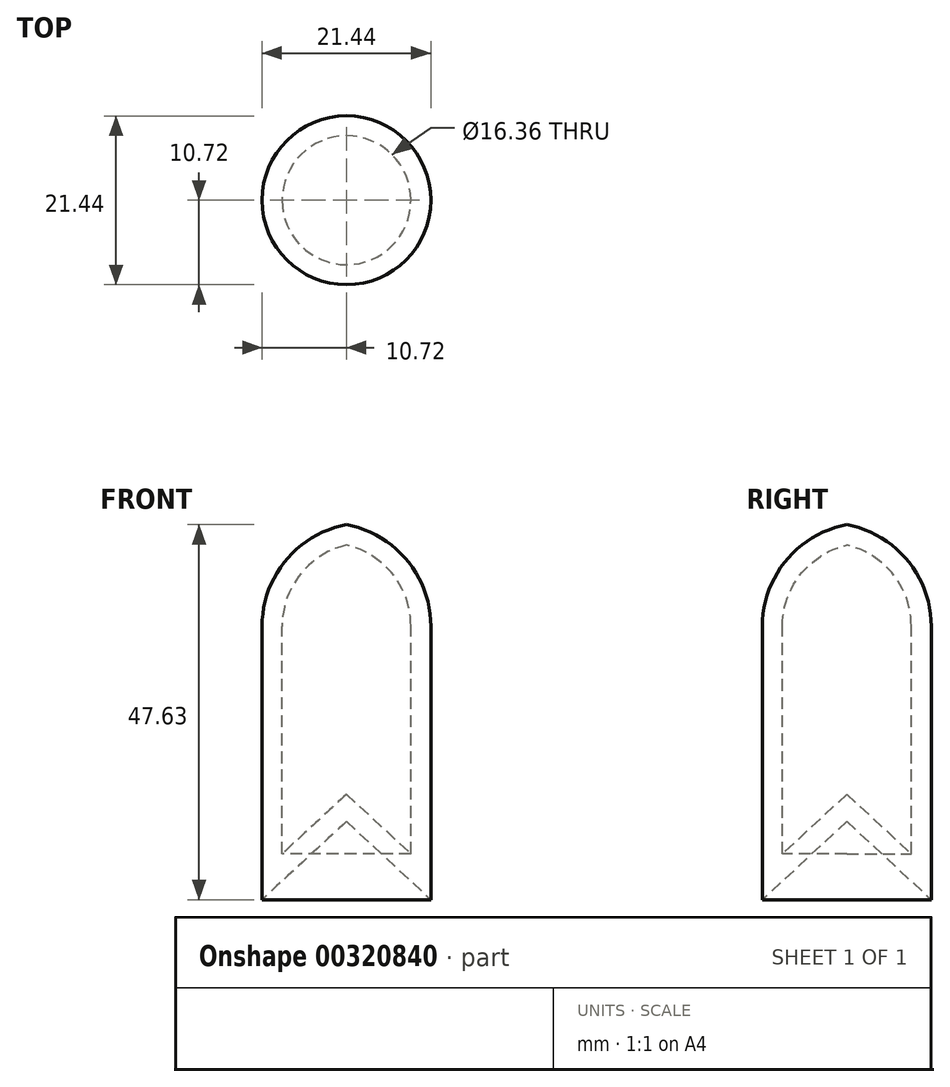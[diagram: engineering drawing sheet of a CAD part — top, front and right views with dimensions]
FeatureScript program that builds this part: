
annotation { "Feature Type Name" : "Feature", "Feature Type Description" : "" }
export const myFeature = defineFeature(function(context is Context, id is Id, definition is map)
    precondition{}
    {
        {
            var Q0;
            Q0=qCreatedBy(makeId("Front.planeOp"),FACE);
            var sketch = newSketch(context, id + "F0", { "sketchPlane" : qUnion([Q0])});
            skLineSegment(sketch, "E0", {"start": v(0, 0) * mm, "end": v(8.18, -7.58) * mm});
            skLineSegment(sketch, "E1", {"start": v(8.18, -7.58) * mm, "end": v(8.18, 21.34) * mm});
            skArc(sketch, "E2", {"start": v(8.18, 21.34) * mm, "mid": v(5.89, 27.92) * mm, "end": v(0, 31.65) * mm});
            skArc(sketch, "E3.0", {"start": v(10.72, 21.34) * mm, "mid": v(7.7, 29.73) * mm, "end": v(0, 34.24) * mm});
            skLineSegment(sketch, "E3.1", {"start": v(10.72, -13.39) * mm, "end": v(10.72, 21.34) * mm});
            skLineSegment(sketch, "E3.2", {"start": v(0, -3.46) * mm, "end": v(10.72, -13.39) * mm});
            skLineSegment(sketch, "E4", {"start": v(0, 34.24) * mm, "end": v(0, 31.65) * mm});
            skLineSegment(sketch, "E5", {"start": v(0, 0) * mm, "end": v(0, -3.46) * mm});
            skSolve(sketch);
        }
        {
            var Q0;
            Q0 = qSketchRegion(id + "F0", true);
            var Q1;
            Q1=sQuery(id+"F0.wireOp",EDGE,"E5");
            revolve(context, id + "F1", {"entities" : qUnion([Q0]), "axis" : qUnion([Q1]), "revolveType" : RevolveType.FULL});
        }
    });
